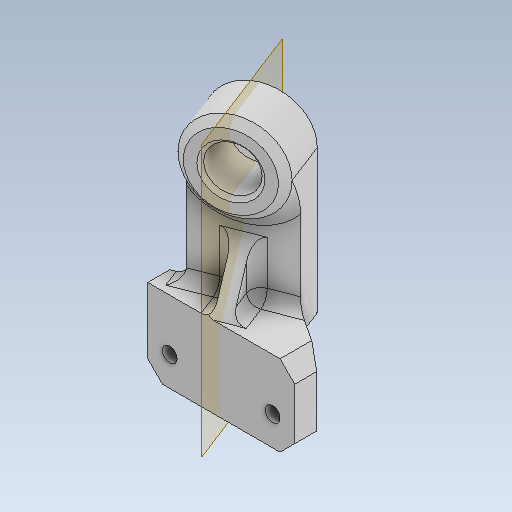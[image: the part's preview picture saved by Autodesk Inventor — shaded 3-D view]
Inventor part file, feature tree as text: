
AUTODESK INVENTOR PART (.ipt)
format: ipt  version: 2023 (Build 270158000, 158)  size: 240,128 bytes
history: native  units: mm
features: sketch x12, other x3, plane x1
ambient origin geometry x8: Origin, YZ Plane, XZ Plane, XY Plane, X Axis, Y Axis, Z Axis, Center Point
bodies: Solid1 (feature_tree)
feature tree (16):
  other  "body_conn_2.ipt"
  other  "Solid1::body_conn_2.ipt"
  other  "TaggingFeature1"
  sketch  "Sketch1"  dims[d0=10.0mm]
  sketch  "Sketch2"
  sketch  "Sketch3"
  sketch  "Sketch4"
  sketch  "Sketch5"
  sketch  "Sketch6"
  sketch  "Sketch7"
  sketch  "Sketch9"
  sketch  "Sketch10"
  sketch  "Sketch11"
  sketch  "Sketch12"
  sketch  "Sketch13"
  plane  "Work Plane1"
